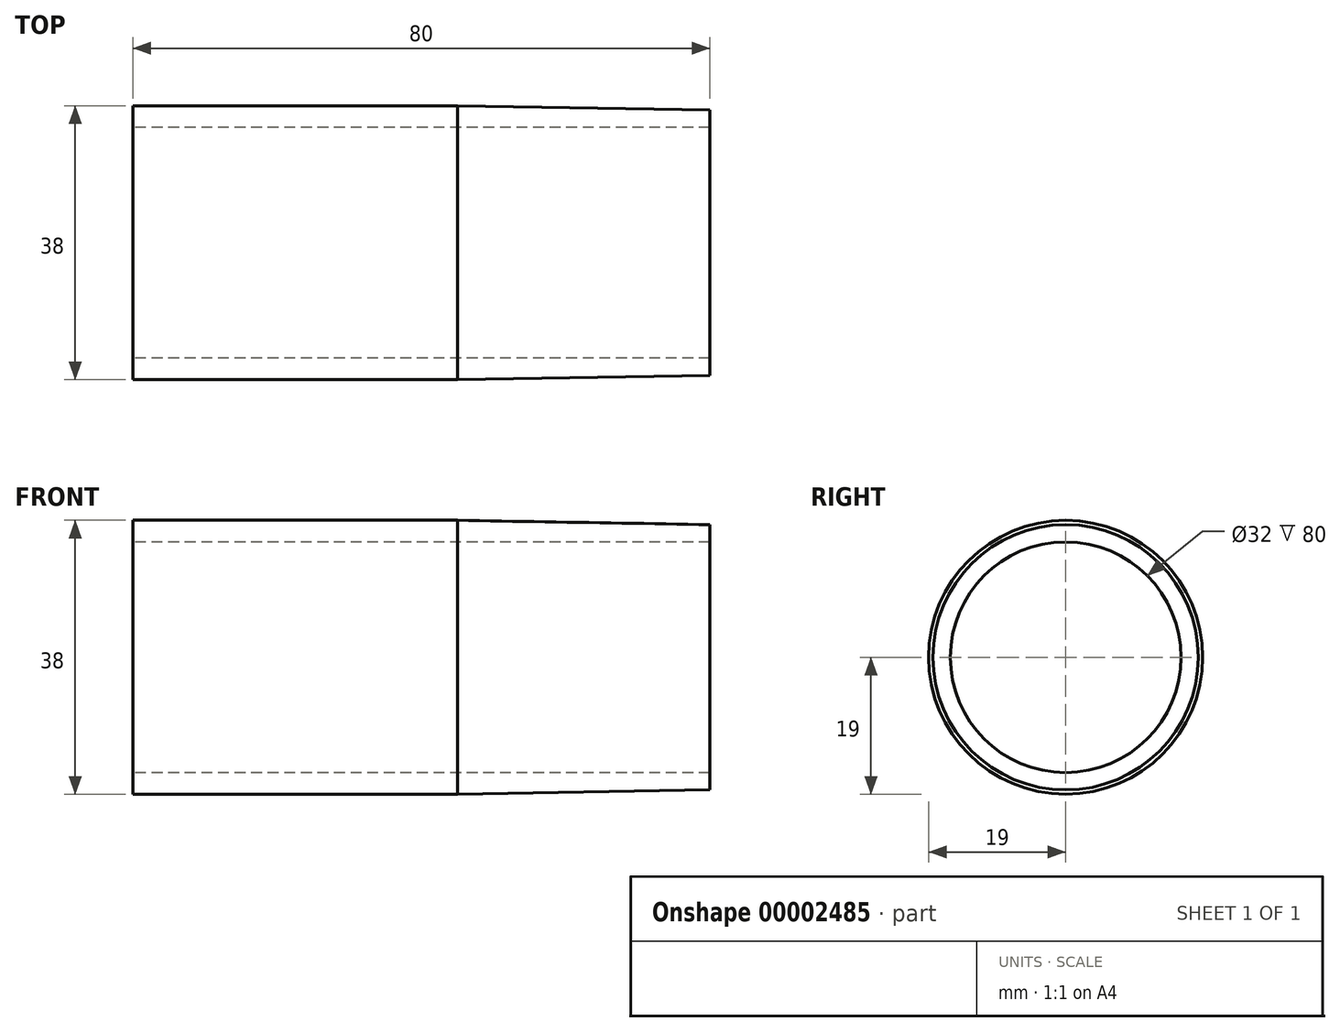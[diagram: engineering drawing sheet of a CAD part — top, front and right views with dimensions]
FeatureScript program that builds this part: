
annotation { "Feature Type Name" : "Feature", "Feature Type Description" : "" }
export const myFeature = defineFeature(function(context is Context, id is Id, definition is map)
    precondition{}
    {
        {
            var Q0;
            Q0=qCreatedBy(makeId("Front.planeOp"),FACE);
            var sketch = newSketch(context, id + "F0", { "sketchPlane" : qUnion([Q0])});
            skLineSegment(sketch, "E0", {"start": v(-117.71, 0) * mm, "end": v(110.04, 0) * mm, "construction": true});
            skLineSegment(sketch, "E1.bottom", {"start": v(-45, 19) * mm, "end": v(0, 19) * mm});
            skLineSegment(sketch, "E1.top", {"start": v(-45, 16) * mm, "end": v(35, 16) * mm});
            skLineSegment(sketch, "E1.left", {"start": v(-45, 19) * mm, "end": v(-45, 16) * mm});
            skLineSegment(sketch, "E2", {"start": v(0, 19) * mm, "end": v(35, 18.4) * mm});
            skLineSegment(sketch, "E3", {"start": v(35, 18.4) * mm, "end": v(35, 16) * mm});
            skSolve(sketch);
        }
        {
            var Q0;
            Q0=makeQuery(id+"F0.imprint","IMPRINT",FACE,{"disambiguationData":[TD([[makeQuery(id+"F0.imprint","IMPRINT",EDGE,{"derivedFrom":sQuery(id+"F0.wireOp",EDGE,"E1.bottom")}),-1.0]])]});
            var Q1;
            Q1=sQuery(id+"F0.wireOp",EDGE,"E0");
            revolve(context, id + "F1", {"entities" : qUnion([Q0]), "axis" : qUnion([Q1]), "revolveType" : RevolveType.FULL});
        }
    });
